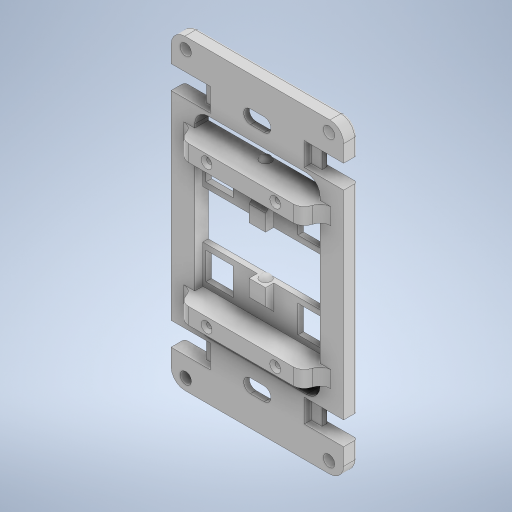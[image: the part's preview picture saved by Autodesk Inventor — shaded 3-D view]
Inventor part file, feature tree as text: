
AUTODESK INVENTOR PART (.ipt)
format: ipt  version: 2023 (Build 270158000, 158)  size: 620,544 bytes
history: native  units: mm
features: extrude x12, sketch x12, fillet x6, other x3, mirror x3, chamfer x2, revolve x1, projected_geometry x1
ambient origin geometry x8: Origin, YZ Plane, XZ Plane, XY Plane, X Axis, Y Axis, Z Axis, Center Point
bodies: Body1 (feature_tree)
feature tree (40):
  other  "솔리드1"
  extrude  "돌출1"  Depth=63.1mm
  extrude  "돌출2"  Depth=112.2mm
  extrude  "돌출3"  Depth=45.85mm
  fillet  "모깎기1"  Radius=70.23mm
  sketch  "스케치4"
  extrude  "돌출4"  Depth=5.0mm TaperAngle=0.0deg
  extrude  "돌출5"  Depth=5.0mm
  mirror  "미러1"
  mirror  "미러2"
  extrude  "돌출6"  Depth=5.0mm
  fillet  "모깎기2"  Radius=5.0mm
  mirror  "미러3"
  fillet  "모깎기3"  Radius=10.0mm
  other  "작업 평면1"
  sketch  "스케치9"
  extrude  "돌출8"  Depth=104.0mm
  extrude  "돌출9"  Depth=4.2mm
  fillet  "모깎기7"  Radius=52.4mm
  chamfer  "모따기1"  [1 undecoded]
  other  "작업 평면2"
  extrude  "돌출10"  Depth=5.0mm
  fillet  "모깎기9"  Radius=7.0mm
  fillet  "모깎기10"  Radius=8.5mm
  extrude  "돌출11"  Depth=3.4mm
  extrude  "돌출12"  Depth=11.2mm
  chamfer  "모따기2"  Distance=4.0mm
  revolve  "회전3"
  sketch  "스케치18"
  extrude  "돌출13"  TaperAngle=0.0deg  [1 undecoded]
  sketch  "스케치1"
  sketch  "스케치2"
  sketch  "스케치3"
  sketch  "스케치6"
  projected_geometry  "투영된 루프1"
  sketch  "스케치13"
  sketch  "스케치15"
  sketch  "스케치16"
  sketch  "스케치17"
  sketch  "스케치19"
note: 2 required parameter values undecoded (feature->parameter linkage not recoverable at this tier; creation-order binding heuristic only, values carry confidence <= 0.55)
